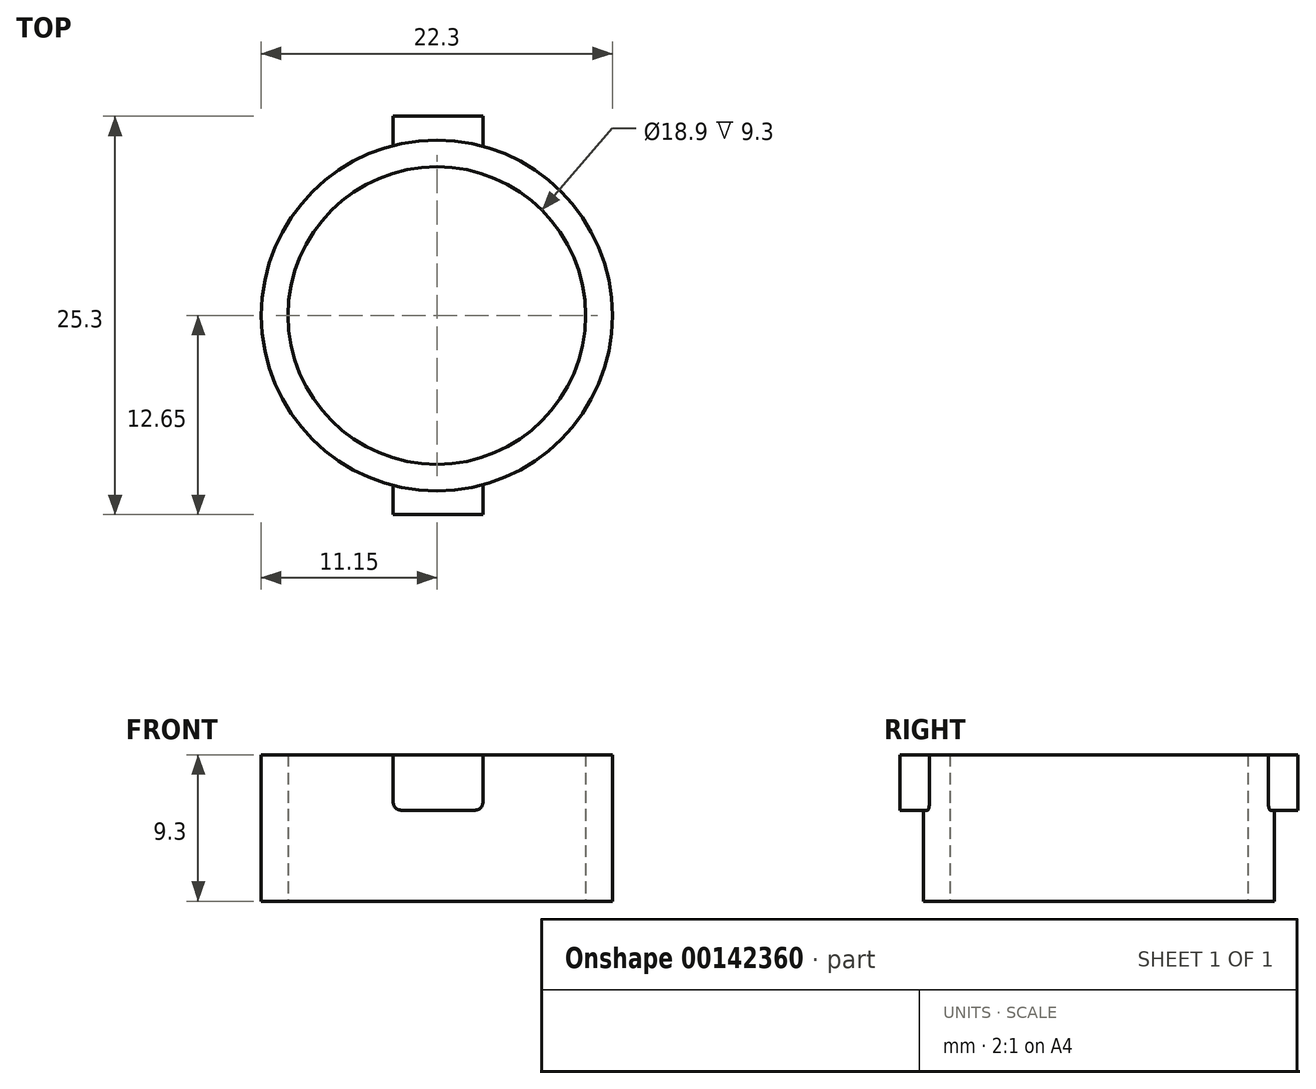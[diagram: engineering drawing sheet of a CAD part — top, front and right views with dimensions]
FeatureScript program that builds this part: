
annotation { "Feature Type Name" : "Feature", "Feature Type Description" : "" }
export const myFeature = defineFeature(function(context is Context, id is Id, definition is map)
    precondition{}
    {
        {
            var Q0;
            Q0=qCreatedBy(makeId("Top.planeOp"),FACE);
            var sketch = newSketch(context, id + "F0", { "sketchPlane" : qUnion([Q0])});
            skCircle(sketch, "E0", {"center": v(0, 0) * mm, "radius": 9.45 * mm});
            skCircle(sketch, "E1", {"center": v(0, 0) * mm, "radius": 11.15 * mm});
            skSolve(sketch);
        }
        {
            var Q0;
            Q0=makeQuery(id+"F0.imprint","IMPRINT",FACE,{"disambiguationData":[TD([[makeQuery(id+"F0.imprint","IMPRINT",EDGE,{"derivedFrom":sQuery(id+"F0.wireOp",EDGE,"E0")}),-1.0]])]});
            extrude(context, id + "F1", {"entities" : qUnion([Q0]), "depth" : 9.3 * mm});
        }
        {
            var Q0;
            Q0=qCreatedBy(makeId("Front.planeOp"),FACE);
            cPlane(context, id + "F2", {"entities" : qUnion([Q0]), "cplaneType" : CPlaneType.OFFSET, "offset" : 11.15 * mm, "width" : 150 * mm, "height" : 150 * mm});
        }
        {
            var Q0;
            Q0=qCreatedBy(id+"F2.planeOp",FACE);
            var sketch = newSketch(context, id + "F3", { "sketchPlane" : qUnion([Q0])});
            skLineSegment(sketch, "E2.bottom", {"start": v(-2.77, 9.28) * mm, "end": v(2.93, 9.28) * mm});
            skLineSegment(sketch, "E2.top", {"start": v(-2.77, 5.78) * mm, "end": v(2.93, 5.78) * mm});
            skLineSegment(sketch, "E2.left", {"start": v(-2.77, 9.28) * mm, "end": v(-2.77, 5.78) * mm});
            skLineSegment(sketch, "E2.right", {"start": v(2.93, 9.28) * mm, "end": v(2.93, 5.78) * mm});
            skSolve(sketch);
        }
        {
            var Q0;
            Q0=makeQuery(id+"F3.imprint","IMPRINT",FACE,{"disambiguationData":[TD([[makeQuery(id+"F3.imprint","IMPRINT",EDGE,{"derivedFrom":sQuery(id+"F3.wireOp",EDGE,"E2.bottom")}),-1.0]])]});
            extrude(context, id + "F4", {"entities" : qUnion([Q0]), "depth" : 3 * mm, "symmetric" : true});
        }
        {
            var Q0;
            Q0=makeQuery(id+"F4.opExtrude","SWEPT_EDGE",EDGE,{"disambiguationData":[OSD([sQuery(id+"F3.wireOp",EDGE,"E2.top"),sQuery(id+"F3.wireOp",EDGE,"E2.left")])]});
            var Q1;
            Q1=makeQuery(id+"F4.opExtrude","SWEPT_EDGE",EDGE,{"disambiguationData":[OSD([sQuery(id+"F3.wireOp",EDGE,"E2.top"),sQuery(id+"F3.wireOp",EDGE,"E2.right")])]});
            fillet(context, id + "F5", {"entities" : qUnion([Q0, Q1]), "radius" : 0.5 * mm, "tangentPropagation" : true, "allowEdgeOverflow" : false});
        }
        {
            var Q0;
            Q0=makeQuery(id+"F4.opExtrude","SWEPT_BODY",BODY,{"disambiguationData":[OSD([sQuery(id+"F3.wireOp",EDGE,"E2.bottom"),sQuery(id+"F3.wireOp",EDGE,"E2.top"),sQuery(id+"F3.wireOp",EDGE,"E2.left"),sQuery(id+"F3.wireOp",EDGE,"E2.right")])]});
            var Q1;
            Q1=qCreatedBy(makeId("Front.planeOp"),FACE);
            mirror(context, id + "F6", {"operationType" : NewBodyOperationType.ADD, "entities" : qUnion([Q0]), "mirrorPlane" : qUnion([Q1])});
        }
    });
